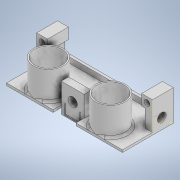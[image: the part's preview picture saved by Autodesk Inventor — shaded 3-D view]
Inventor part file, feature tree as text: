
AUTODESK INVENTOR PART (.ipt)
format: ipt  version: 2020.1 (Build 241239000, 239)  size: 427,520 bytes
history: native  units: mm
features: sketch x27, extrude x20, fillet x4
ambient origin geometry x8: Origin, YZ Plane, XZ Plane, XY Plane, X Axis, Y Axis, Z Axis, Center Point
bodies: Solid1 (feature_tree)
feature tree (51):
  sketch  "Sketch1"  dims[d3=25.4mm d4=25.4mm]
  extrude  "Extrusion1"  Depth=25.4mm
  extrude  "Extrusion2"  Depth=10.0mm TaperAngle=0.0deg
  extrude  "Extrusion3"  Depth=15.0mm
  sketch  "Sketch5"  dims[d14=14.85mm d15=0.0mm d18=2.0mm]
  extrude  "Extrusion4"  Depth=25.4mm TaperAngle=0.0deg
  sketch  "Sketch8"  dims[d24=10.0mm d25=0.0mm d26=15.0mm]
  extrude  "Extrusion5"  Depth=2.0mm
  extrude  "Extrusion6"  Depth=10.0mm TaperAngle=0.0deg
  sketch  "Sketch11"  dims[d32=25.4mm d33=0.0mm d34=7.4mm]
  extrude  "Extrusion7"  Depth=10.0mm
  extrude  "Extrusion8"  Depth=8.0mm
  extrude  "Extrusion9"  Depth=18.0mm
  sketch  "Sketch14"  dims[d42=25.0mm d43=10.0mm d44=0.0mm]
  extrude  "Extrusion10"  Depth=7.4mm
  extrude  "Extrusion11"  Depth=14.9mm TaperAngle=0.0deg
  sketch  "Sketch19"  dims[d58=1.5875mm d59=1.5875mm]
  sketch  "Sketch20"  dims[d60=1.5875mm d61=6.35mm]
  extrude  "Extrusion12"  Depth=20.0mm TaperAngle=0.0deg
  extrude  "Extrusion13"  Depth=10.0mm TaperAngle=0.0deg
  sketch  "Sketch23"  dims[d71=0.5mm d72=0.0mm d74=41.5mm d75=3.25mm d76=0.0mm d78=38.0mm]
  sketch  "Sketch24"  dims[d79=39.0mm d80=0.0mm]
  extrude  "Extrusion14"  Depth=10.0mm TaperAngle=0.0deg
  extrude  "Extrusion15"  Depth=10.0mm TaperAngle=0.0deg
  fillet  "Fillet1"  Radius=21.0mm
  sketch  "Sketch26"  dims[d82=3.5mm d83=0.0mm]
  extrude  "Extrusion16"  Depth=1.5875mm
  extrude  "Extrusion17"  Depth=6.35mm
  extrude  "Extrusion18"  Depth=20.0mm TaperAngle=0.0deg
  fillet  "Fillet2"  Radius=15.0mm
  extrude  "Extrusion19"  Depth=41.5mm
  extrude  "Extrusion20"  Depth=41.5mm
  fillet  "Fillet3"  Radius=3.25mm
  fillet  "Fillet4"  Radius=38.0mm
  sketch  "Sketch2"  dims[d5=12.7mm d6=10.0mm d7=0.0mm]
  sketch  "Sketch3"  dims[d8=15.0mm d9=15.0mm]
  sketch  "Sketch4"  dims[d10=8.0mm d11=25.4mm d12=0.0mm]
  sketch  "Sketch7"  dims[d19=3.25mm d20=150.0mm d21=10.0mm d22=0.0mm d23=0.0mm]
  sketch  "Sketch9"  dims[d27=15.0mm d28=8.0mm]
  sketch  "Sketch10"  dims[d29=25.4mm d30=0.0mm d31=18.0mm]
  sketch  "Sketch12"  dims[d35=14.9mm d36=0.0mm d37=14.9mm d38=0.0mm]
  sketch  "Sketch13"  dims[d39=31.75mm d40=20.0mm d41=0.0mm]
  sketch  "Sketch17"  dims[d45=31.75mm d46=10.0mm d47=0.0mm]
  sketch  "Sketch18"  dims[d48=12.7mm d49=10.0mm d50=0.0mm d51=21.0mm]
  sketch  "Sketch21"  dims[d63=8.0mm d64=20.0mm d65=0.0mm d66=15.0mm d67=0.0mm]
  sketch  "Sketch22"  dims[d68=9.0mm d70=41.5mm]
  sketch  "Sketch25"  dims[d81=3.0mm]
  sketch  "Sketch27"  dims[d84=2.25mm]
  sketch  "Sketch28"  dims[d85=2.25mm]
  sketch  "Sketch29"  dims[d86=3.5mm d87=0.0mm]
  sketch  "Sketch30"  dims[d88=1.1mm d89=1.1mm d73=0.5mm]
